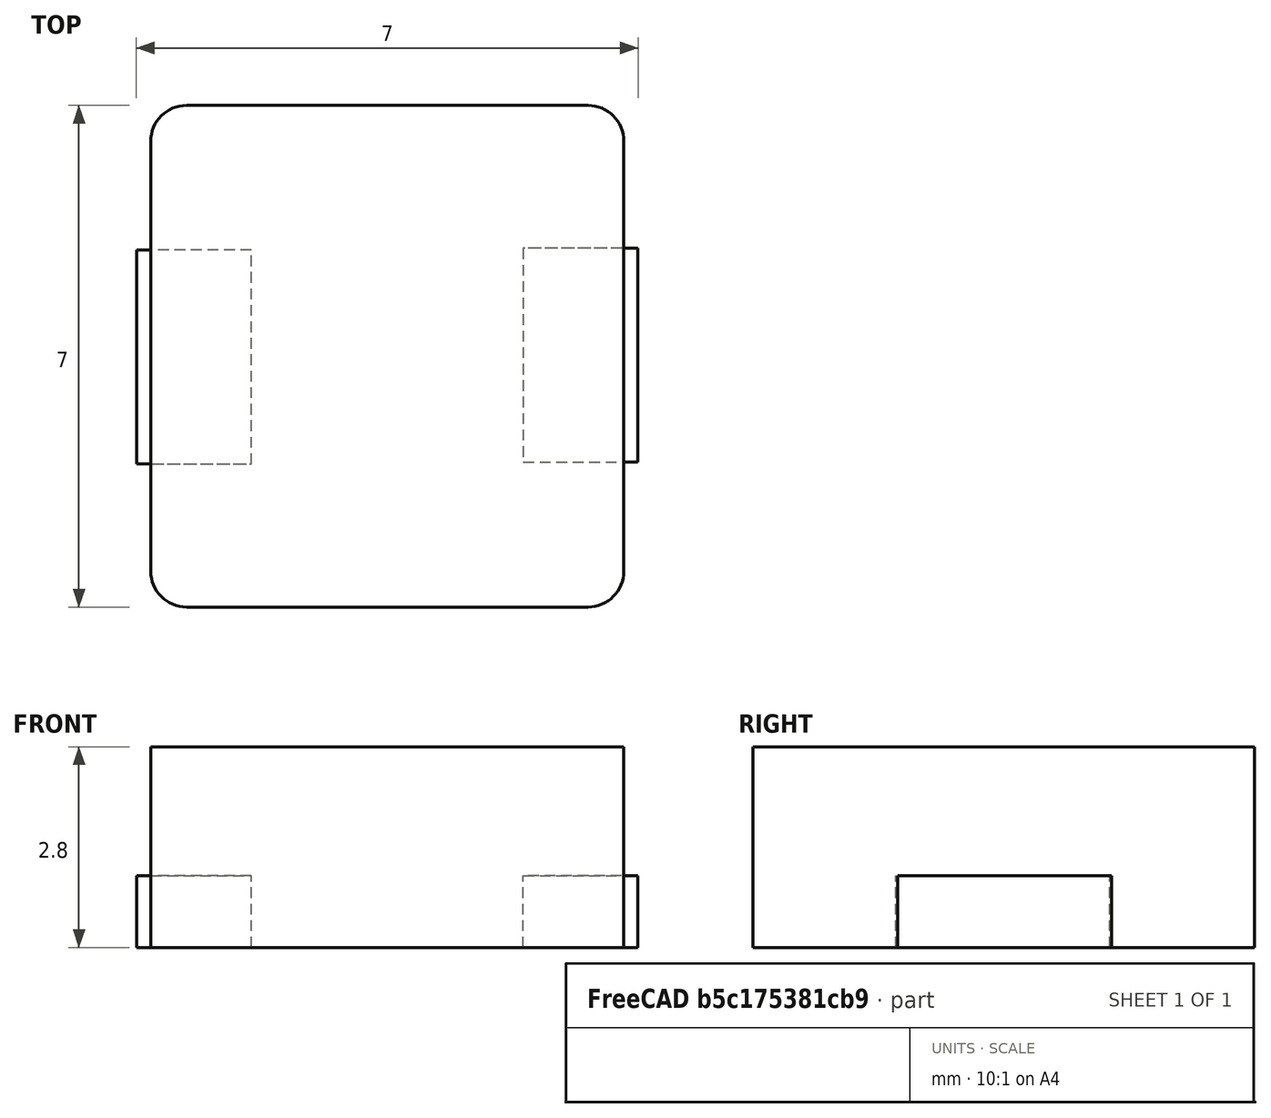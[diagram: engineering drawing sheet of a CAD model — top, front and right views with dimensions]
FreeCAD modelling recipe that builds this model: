
FCSTD DOCUMENT  (FreeCAD 0.19R24276 (Git))
Label: L_Sunking_MWSA0603S
License: All rights reserved
LicenseURL: http://en.wikipedia.org/wiki/All_rights_reserved
objects: Part::Part2DObjectPython×4, Part::Extrusion×2, Part::Box×1, Part::Fillet×1, App::Part×1
note: 8 computed .brp shape members not serialized (recipe doc carries the construction recipe); baked Part::Feature solids carry a one-line shape summary decoded from their .brp

FEATURE [Part::Box] Box  label="Würfel"
  AttacherType = Attacher::AttachEngine3D
  Height = 2.8
  Length = 6.6
  Placement = pos=(-3.3,-3.5,0) rot=(0,0,1;0rad)
  Width = 7
FEATURE [Part::Fillet] Fillet
  Base = -> Box
  Edges = 4 edges r=0.5: [Edge1,Edge3,Edge5,Edge7]
FEATURE [Part::Part2DObjectPython] Rectangle  # Draft 2D object (typed FeaturePython)
  Area = 4.77329
  ChamferSize = 0
  Columns = 1
  FilletRadius = 0
  Height = 2.98439
  Length = 1.59942
  MakeFace = true
  Placement = pos=(1.89778,-1.47967,0) rot=(0,0,1;0rad)
  Rows = 1
FEATURE [Part::Extrusion] Extrude
  Base = -> Rectangle
  Dir = (0,0,1)
  DirMode = 2
  FaceMakerClass = Part::FaceMakerBullseye
  LengthFwd = 1
  LengthRev = 0
  Solid = true
  Symmetric = false
FEATURE [Part::Part2DObjectPython] Rectangle001  # Draft 2D object (typed FeaturePython)
  Area = 4.77329
  ChamferSize = 0
  Columns = 1
  FilletRadius = 0
  Height = 2.98439
  Length = 1.59942
  MakeFace = true
  Placement = pos=(1.89778,-1.47967,0) rot=(0,0,1;0rad)
  Rows = 1
FEATURE [Part::Part2DObjectPython] Rectangle002  # Draft 2D object (typed FeaturePython)
  Area = 4.77329
  ChamferSize = 0
  Columns = 1
  FilletRadius = 0
  Height = 2.98439
  Length = 1.59942
  MakeFace = true
  Placement = pos=(1.89778,-1.47967,0) rot=(0,0,1;0rad)
  Rows = 1
FEATURE [Part::Extrusion] Extrude001
  Base = -> Rectangle002
  Dir = (0,0,1)
  DirMode = 2
  FaceMakerClass = Part::FaceMakerBullseye
  LengthFwd = 1
  LengthRev = 0
  Placement = pos=(0,0,0) rot=(0,0,1;3.14159rad)
  Solid = true
  Symmetric = false
FEATURE [Part::Part2DObjectPython] Rectangle003  # Draft 2D object (typed FeaturePython)
  Area = 4.77329
  ChamferSize = 0
  Columns = 1
  FilletRadius = 0
  Height = 2.98439
  Length = 1.59942
  MakeFace = true
  Placement = pos=(1.89778,-1.47967,0) rot=(0,0,1;0rad)
  Rows = 1
FEATURE [App::Part] Part001
  Group = -> [Rectangle,Extrude,Box,Fillet,Rectangle002,Extrude001,Rectangle003]
  Origin = -> Origin001
